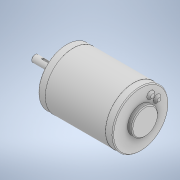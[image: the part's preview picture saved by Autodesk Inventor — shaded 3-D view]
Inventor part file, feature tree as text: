
AUTODESK INVENTOR PART (.ipt)
format: ipt  version: 2020.2 (Build 242310000, 310)  size: 159,232 bytes
history: native  units: in
note: dims shown in document units (in); Inventor stores cm internally (conversion verified against a paired STEP export)
features: chamfer x1
ambient origin geometry x8: Origin, YZ Plane, XZ Plane, XY Plane, X Axis, Y Axis, Z Axis, Center Point
bodies: Solid1 (feature_tree)
feature tree (1):
  chamfer  "Chamfer3"  [1 undecoded]
note: 1 required parameter value undecoded (feature->parameter linkage not recoverable at this tier; creation-order binding heuristic only, values carry confidence <= 0.55)
